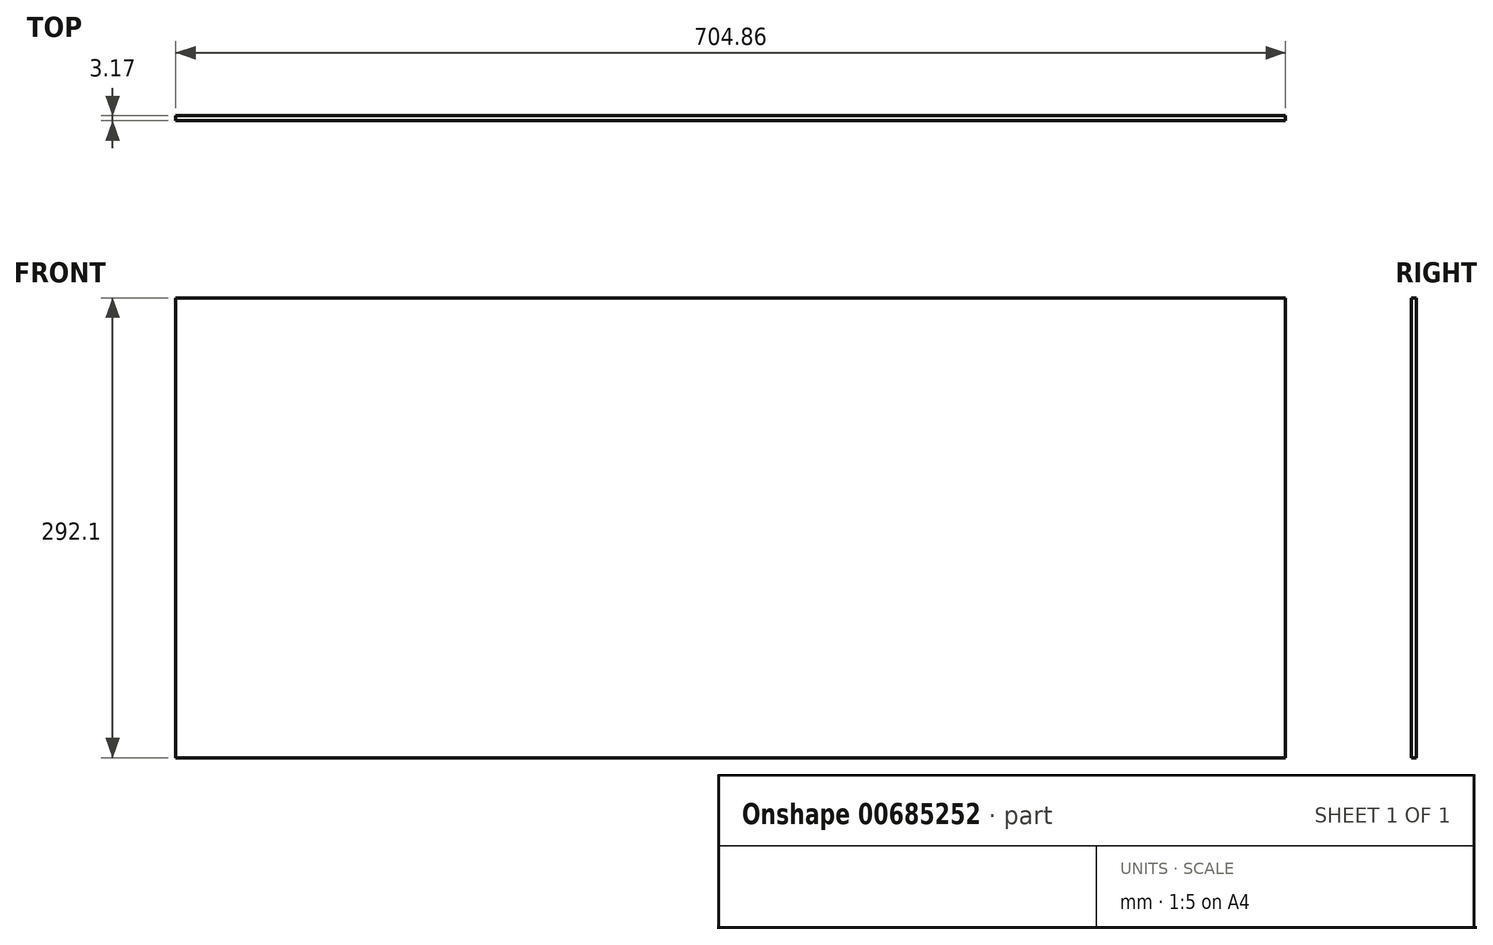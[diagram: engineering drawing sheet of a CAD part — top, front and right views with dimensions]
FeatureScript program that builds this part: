
annotation { "Feature Type Name" : "Feature", "Feature Type Description" : "" }
export const myFeature = defineFeature(function(context is Context, id is Id, definition is map)
    precondition{}
    {
        {
            var Q0;
            Q0=qCreatedBy(makeId("Front.planeOp"),FACE);
            var sketch = newSketch(context, id + "F0", { "sketchPlane" : qUnion([Q0])});
            skLineSegment(sketch, "E0.bottom", {"start": v(352.43, 146.05) * mm, "end": v(-352.43, 146.05) * mm});
            skLineSegment(sketch, "E0.top", {"start": v(352.43, -146.05) * mm, "end": v(-352.43, -146.05) * mm});
            skLineSegment(sketch, "E0.left", {"start": v(352.43, 146.05) * mm, "end": v(352.43, -146.05) * mm});
            skLineSegment(sketch, "E0.right", {"start": v(-352.43, 146.05) * mm, "end": v(-352.43, -146.05) * mm});
            skPoint(sketch, "E0.middle", {"position": v(0, 0) * mm});
            skSolve(sketch);
        }
        {
            var Q0;
            Q0 = qSketchRegion(id + "F0", true);
            extrude(context, id + "F1", {"entities" : qUnion([Q0]), "depth" : 3.17 * mm, "offsetDistance" : 25.4 * mm});
        }
    });
